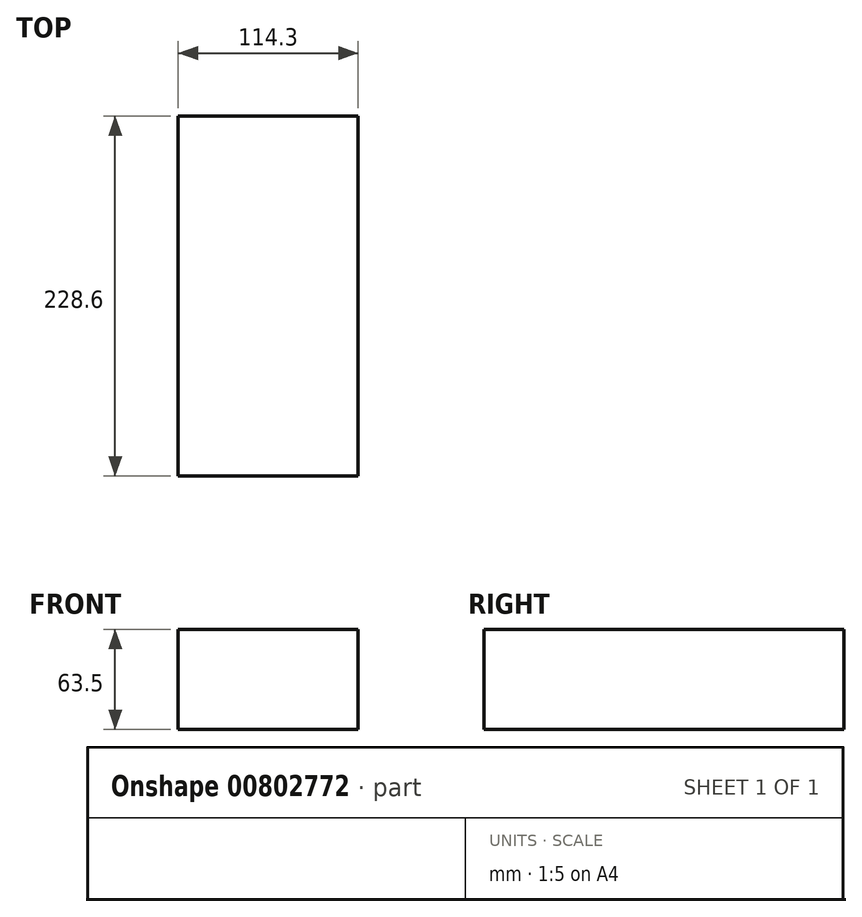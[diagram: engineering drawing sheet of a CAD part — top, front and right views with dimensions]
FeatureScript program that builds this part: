
annotation { "Feature Type Name" : "Feature", "Feature Type Description" : "" }
export const myFeature = defineFeature(function(context is Context, id is Id, definition is map)
    precondition{}
    {
        {
            var Q0;
            Q0=qCreatedBy(makeId("Front.planeOp"),FACE);
            var sketch = newSketch(context, id + "F0", { "sketchPlane" : qUnion([Q0])});
            skLineSegment(sketch, "E0.bottom", {"start": v(57.15, -31.75) * mm, "end": v(-57.15, -31.75) * mm});
            skLineSegment(sketch, "E0.top", {"start": v(57.15, 31.75) * mm, "end": v(-57.15, 31.75) * mm});
            skLineSegment(sketch, "E0.left", {"start": v(57.15, -31.75) * mm, "end": v(57.15, 31.75) * mm});
            skLineSegment(sketch, "E0.right", {"start": v(-57.15, -31.75) * mm, "end": v(-57.15, 31.75) * mm});
            skPoint(sketch, "E0.middle", {"position": v(0, 0) * mm});
            skSolve(sketch);
        }
        {
            var Q0;
            Q0 = qSketchRegion(id + "F0", true);
            extrude(context, id + "F1", {"entities" : qUnion([Q0]), "oppositeDirection" : true, "depth" : 228.6 * mm, "offsetDistance" : 25.4 * mm});
        }
    });
